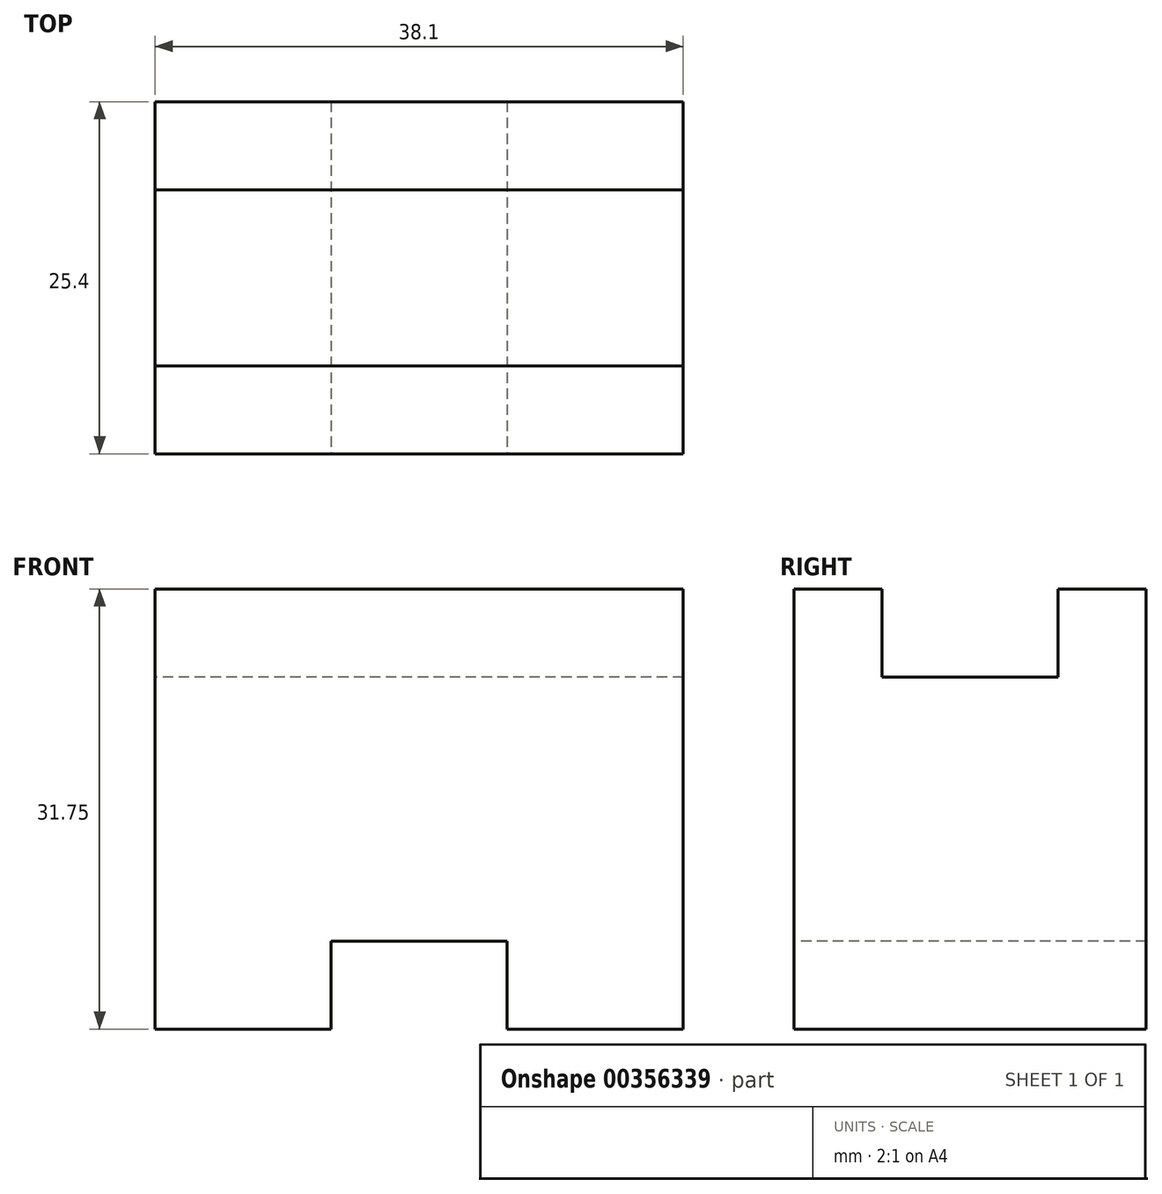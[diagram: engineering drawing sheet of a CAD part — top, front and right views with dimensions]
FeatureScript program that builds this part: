
annotation { "Feature Type Name" : "Feature", "Feature Type Description" : "" }
export const myFeature = defineFeature(function(context is Context, id is Id, definition is map)
    precondition{}
    {
        {
            var Q0;
            Q0=qCreatedBy(makeId("Right.planeOp"),FACE);
            var sketch = newSketch(context, id + "F0", { "sketchPlane" : qUnion([Q0])});
            skLineSegment(sketch, "E0", {"start": v(0, 0) * mm, "end": v(0, 31.75) * mm});
            skLineSegment(sketch, "E1", {"start": v(0, 31.75) * mm, "end": v(6.35, 31.75) * mm});
            skLineSegment(sketch, "E2", {"start": v(6.35, 31.75) * mm, "end": v(6.35, 25.4) * mm});
            skLineSegment(sketch, "E3", {"start": v(6.35, 25.4) * mm, "end": v(19.05, 25.4) * mm});
            skLineSegment(sketch, "E4", {"start": v(19.05, 25.4) * mm, "end": v(19.05, 31.75) * mm});
            skLineSegment(sketch, "E5", {"start": v(19.05, 31.75) * mm, "end": v(25.4, 31.75) * mm});
            skLineSegment(sketch, "E6", {"start": v(25.4, 31.75) * mm, "end": v(25.4, 0) * mm});
            skLineSegment(sketch, "E7", {"start": v(25.4, 0) * mm, "end": v(0, 0) * mm});
            skSolve(sketch);
        }
        {
            var Q0;
            Q0 = qSketchRegion(id + "F0", true);
            extrude(context, id + "F1", {"entities" : qUnion([Q0]), "depth" : 38.1 * mm});
        }
        {
            var Q0;
            Q0=makeQuery(id+"F1.opExtrude","SWEPT_FACE",FACE,{"disambiguationData":[OSD([sQuery(id+"F0.wireOp",EDGE,"E0")])]});
            var sketch = newSketch(context, id + "F2", { "sketchPlane" : qUnion([Q0])});
            skLineSegment(sketch, "E8", {"start": v(12.7, 0) * mm, "end": v(12.7, 6.35) * mm});
            skLineSegment(sketch, "E9", {"start": v(12.7, 6.35) * mm, "end": v(25.4, 6.35) * mm});
            skLineSegment(sketch, "E10", {"start": v(25.4, 6.35) * mm, "end": v(25.4, 0) * mm});
            skLineSegment(sketch, "E11", {"start": v(25.4, 0) * mm, "end": v(12.7, 0) * mm});
            skSolve(sketch);
        }
        {
            var Q0;
            Q0 = qSketchRegion(id + "F2", true);
            extrude(context, id + "F3", {"entities" : qUnion([Q0]), "operationType" : NewBodyOperationType.REMOVE, "oppositeDirection" : true, "depth" : 25.4 * mm});
        }
    });
